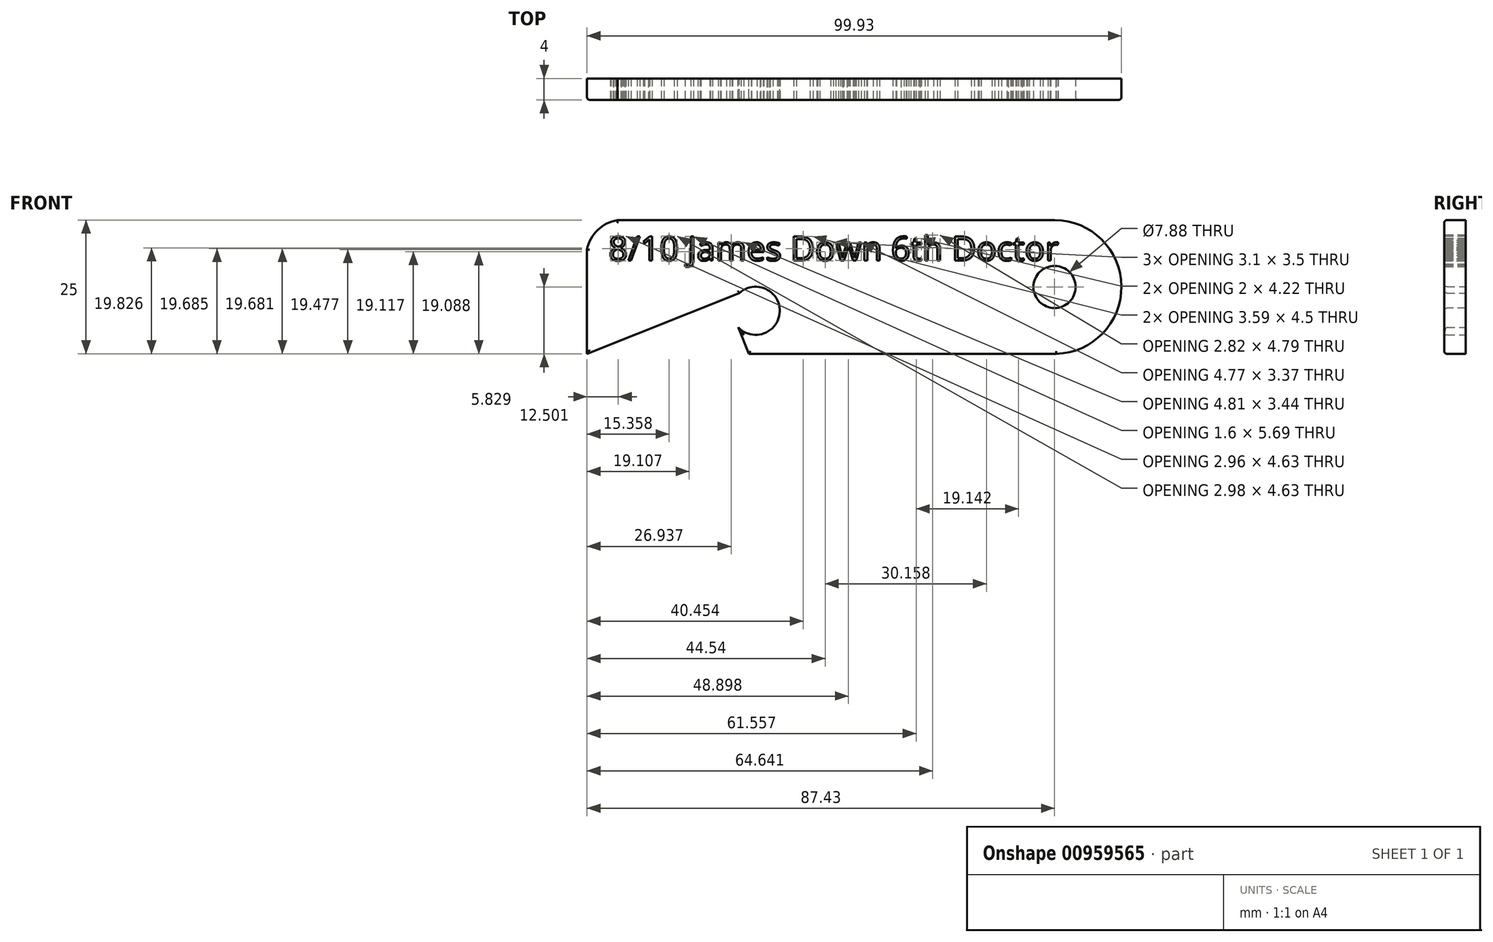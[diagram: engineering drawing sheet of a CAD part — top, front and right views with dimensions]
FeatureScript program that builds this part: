
annotation { "Feature Type Name" : "Feature", "Feature Type Description" : "" }
export const myFeature = defineFeature(function(context is Context, id is Id, definition is map)
    precondition{}
    {
        {
            var Q0;
            Q0=qCreatedBy(makeId("Front.planeOp"),FACE);
            var sketch = newSketch(context, id + "F0", { "sketchPlane" : qUnion([Q0])});
            skLineSegment(sketch, "E0.bottom", {"start": v(-30.33, 12.91) * mm, "end": v(69.67, 12.91) * mm});
            skLineSegment(sketch, "E0.top", {"start": v(-30.33, -12.09) * mm, "end": v(69.67, -12.09) * mm});
            skLineSegment(sketch, "E0.left", {"start": v(-30.33, 12.91) * mm, "end": v(-30.33, -12.09) * mm});
            skLineSegment(sketch, "E0.right", {"start": v(69.67, 12.91) * mm, "end": v(69.67, -12.09) * mm});
            skCircle(sketch, "E1", {"center": v(1.2, -4.04) * mm, "radius": 4.5 * mm});
            skLineSegment(sketch, "E2", {"start": v(-30.33, -12.09) * mm, "end": v(0, 0) * mm});
            skLineSegment(sketch, "E3", {"start": v(-3.3, -4.04) * mm, "end": v(-0.08, -12.09) * mm});
            skSolve(sketch);
        }
        {
            var Q0;
            Q0=makeQuery(id+"F0.imprint","IMPRINT",FACE,{"disambiguationData":[TD([[makeQuery(id+"F0.imprint","IMPRINT",EDGE,{"derivedFrom":sQuery(id+"F0.wireOp",EDGE,"E0.bottom")}),-1.0]])]});
            extrude(context, id + "F1", {"entities" : qUnion([Q0]), "depth" : 4 * mm, "offsetDistance" : 25 * mm});
        }
        {
            var Q0;
            Q0=makeQuery(id+"F1.opExtrude","CAP_FACE",FACE,{"disambiguationData":[OSD([sQuery(id+"F0.wireOp",EDGE,"E0.bottom"),sQuery(id+"F0.wireOp",EDGE,"E0.top"),sQuery(id+"F0.wireOp",EDGE,"E0.left"),sQuery(id+"F0.wireOp",EDGE,"E0.right")])],"isStart":false});
            var sketch = newSketch(context, id + "F2", { "sketchPlane" : qUnion([Q0])});
            skArc(sketch, "E4", {"start": v(57.41, -12.09) * mm, "mid": v(69.6, 0.55) * mm, "end": v(57.14, 12.91) * mm});
            skCircle(sketch, "E5", {"center": v(57.1, 0.41) * mm, "radius": 3.94 * mm});
            skArc(sketch, "E6", {"start": v(-24.64, 12.91) * mm, "mid": v(-29.27, 9.94) * mm, "end": v(-30.33, 4.54) * mm});
            skSolve(sketch);
        }
        {
            var Q0;
            Q0 = qSketchRegion(id + "F2", true);
            var Q1;
            {var subQ0=sQuery(id+"F2.wireOp",EDGE,"E4");Q1=makeQuery(id+"F2.imprint","IMPRINT",FACE,{"disambiguationData":[TD([[makeQuery(id+"F2.imprint","IMPRINT",EDGE,{"derivedFrom":subQ0}),-1.0]])]});}
            var Q2;
            {var subQ0=sQuery(id+"F2.wireOp",EDGE,"E6");var subQ1=makeQuery(id+"F1.opExtrude","CAP_EDGE",EDGE,{"disambiguationData":[OSD([sQuery(id+"F0.wireOp",EDGE,"E0.bottom")])],"isStart":false});var subQ2=makeQuery(id+"F2.imprint","INTERSECT",VERTEX,{"derivedFrom":[subQ1,subQ0]});Q2=makeQuery(id+"F2.imprint","IMPRINT",FACE,{"disambiguationData":[TD([[makeQuery(id+"F2.imprint","IMPRINT",EDGE,{"disambiguationData":[TD([[subQ2,-1.0]])],"derivedFrom":subQ0}),-1.0]])]});}
            extrude(context, id + "F3", {"entities" : qUnion([Q0, Q1, Q2]), "operationType" : NewBodyOperationType.REMOVE, "endBound" : BoundingType.THROUGH_ALL, "oppositeDirection" : true, "depth" : 25 * mm, "offsetDistance" : 25 * mm});
        }
        {
            var Q0;
            Q0=makeQuery(id+"F1.opExtrude","CAP_FACE",FACE,{"disambiguationData":[OSD([sQuery(id+"F0.wireOp",EDGE,"E0.bottom"),sQuery(id+"F0.wireOp",EDGE,"E0.top"),sQuery(id+"F0.wireOp",EDGE,"E0.left"),sQuery(id+"F0.wireOp",EDGE,"E0.right"),sQuery(id+"F0.wireOp",EDGE,"E1"),sQuery(id+"F0.wireOp",EDGE,"E2"),sQuery(id+"F0.wireOp",EDGE,"E3")])],"isStart":false});
            fillet(context, id + "F4", {"entities" : qUnion([Q0]), "radius" : .5 * mm, "tangentPropagation" : true, "allowEdgeOverflow" : false});
        }
        {
            var Q0;
            Q0=makeQuery(id+"F1.opExtrude","CAP_FACE",FACE,{"disambiguationData":[OSD([sQuery(id+"F0.wireOp",EDGE,"E0.bottom"),sQuery(id+"F0.wireOp",EDGE,"E0.top"),sQuery(id+"F0.wireOp",EDGE,"E0.left"),sQuery(id+"F0.wireOp",EDGE,"E0.right"),sQuery(id+"F0.wireOp",EDGE,"E1"),sQuery(id+"F0.wireOp",EDGE,"E2"),sQuery(id+"F0.wireOp",EDGE,"E3")])],"isStart":false});
            var sketch = newSketch(context, id + "F5", { "sketchPlane" : qUnion([Q0])});
            skText(sketch, "E7", { "text": "8/10 James Down 6th Doctor", "fontName": "OpenSans-Regular.ttf"});
            const initialGuessF5  = {"E7": [-0.0263, 0.00534, 1, 0, 0.00454]};
            skSetInitialGuess(sketch, initialGuessF5);
            skSolve(sketch);
        }
        {
            var Q0;
            Q0 = qSketchRegion(id + "F5", true);
            extrude(context, id + "F6", {"entities" : qUnion([Q0]), "operationType" : NewBodyOperationType.REMOVE, "endBound" : BoundingType.THROUGH_ALL, "oppositeDirection" : true, "depth" : 1 * mm, "offsetDistance" : 25 * mm});
        }
    });
